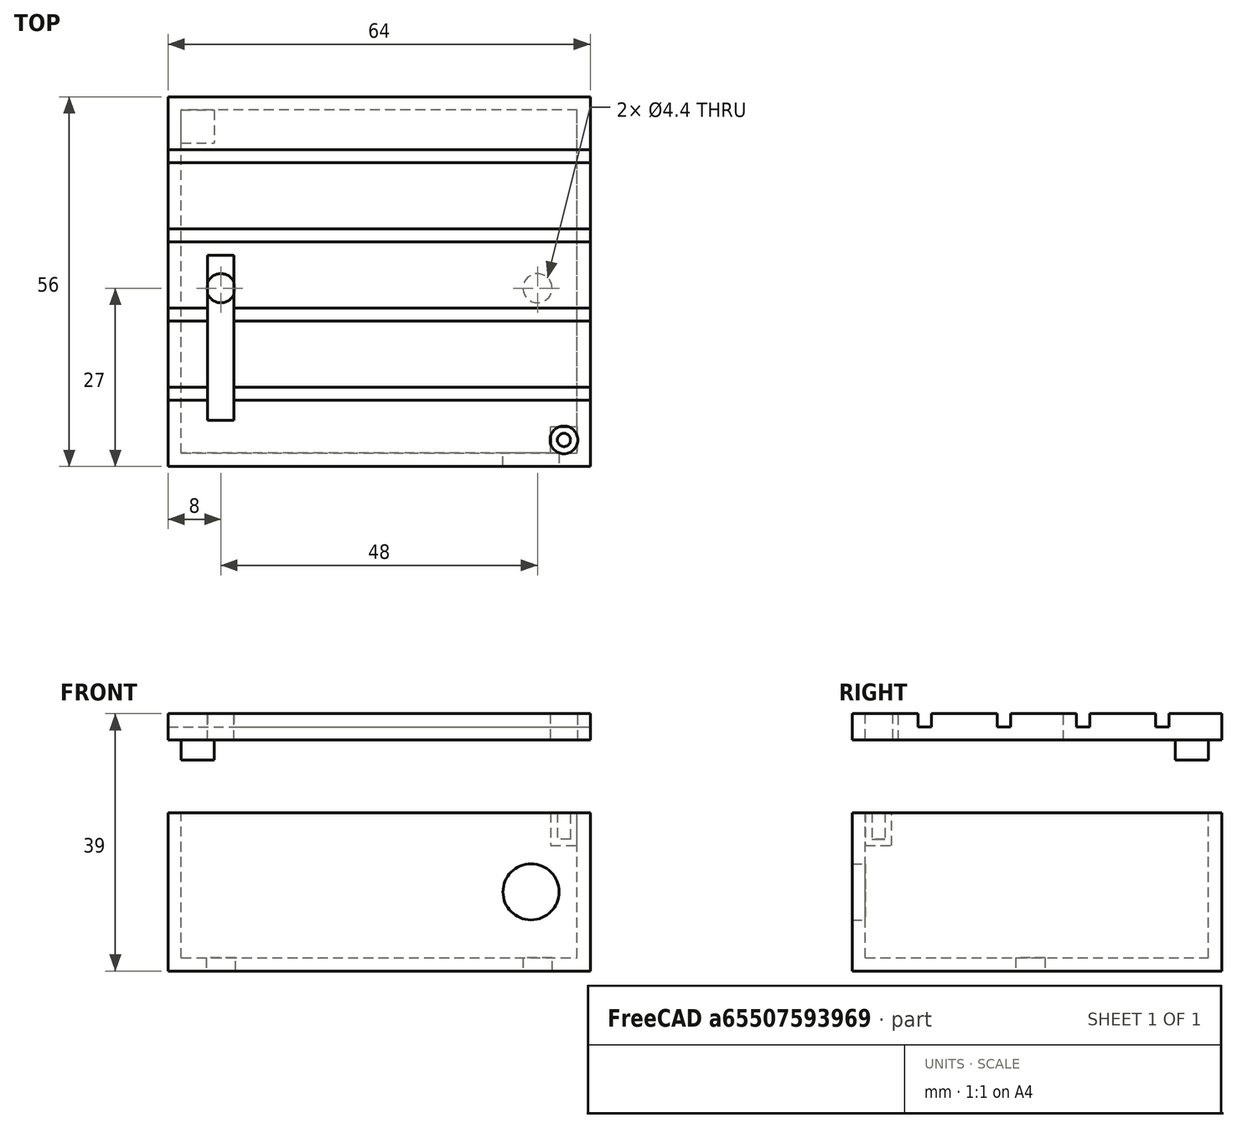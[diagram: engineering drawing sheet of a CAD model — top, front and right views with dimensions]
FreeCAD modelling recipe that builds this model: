
FCSTD DOCUMENT  (FreeCAD 0.20R29603 (Git))
Label: boxv1
License: All rights reserved
LicenseURL: http://en.wikipedia.org/wiki/All_rights_reserved
objects: Part::Box×11, Part::Cut×7, Part::Cylinder×5, Part::MultiFuse×2, App::DocumentObjectGroup×2
note: 25 computed .brp shape members not serialized (recipe doc carries the construction recipe); baked Part::Feature solids carry a one-line shape summary decoded from their .brp

FEATURE [Part::Box] Box  label="Cube"
  AttacherType = Attacher::AttachEngine3D
  Height = 24
  Length = 64
  Width = 56
FEATURE [Part::Box] Box001  label="Cube001"
  AttacherType = Attacher::AttachEngine3D
  Height = 24
  Length = 60
  Placement = pos=(2,2,2) rot=(0,0,1;0rad)
  Width = 52
FEATURE [Part::Cut] Cut
  Base = -> Box
  Tool = -> Box001
FEATURE [Part::Cylinder] Cylinder
  Angle = 360
  AttacherType = Attacher::AttachEngine3D
  FirstAngle = 0
  Height = 10
  Placement = pos=(55,4,12) rot=(1,0,0;1.5708rad)
  Radius = 4.25
  SecondAngle = 0
FEATURE [Part::Box] Box002  label="Cube002"
  AttacherType = Attacher::AttachEngine3D
  Height = 2
  Length = 64
  Placement = pos=(0,0,34) rot=(0,0,1;0rad)
  Width = 56
FEATURE [Part::Cut] Cut001
  Base = -> Cut
  Tool = -> Cylinder
FEATURE [Part::Box] Box003  label="Cube003"
  AttacherType = Attacher::AttachEngine3D
  Height = 5
  Length = 5
  Placement = pos=(2,49,31) rot=(0,0,1;0rad)
  Width = 5
FEATURE [Part::Box] Box004  label="Cube004"
  AttacherType = Attacher::AttachEngine3D
  Height = 5
  Length = 5
  Placement = pos=(58,1,19) rot=(0,0,1;0rad)
  Width = 5
FEATURE [Part::Cylinder] Cylinder001
  Angle = 360
  AttacherType = Attacher::AttachEngine3D
  FirstAngle = 0
  Height = 10
  Placement = pos=(60,4,30) rot=(0,0,1;0rad)
  Radius = 2.1
  SecondAngle = 0
FEATURE [Part::Box] Box005  label="Cube005"
  AttacherType = Attacher::AttachEngine3D
  Height = 10
  Length = 4
  Placement = pos=(6,7,33) rot=(0,0,1;0rad)
  Width = 25
FEATURE [Part::Cylinder] Cylinder002
  Angle = 360
  AttacherType = Attacher::AttachEngine3D
  FirstAngle = 0
  Height = 10
  Placement = pos=(60,4,20) rot=(0,0,1;0rad)
  Radius = 1
  SecondAngle = 0
FEATURE [Part::MultiFuse] Fusion001
  Shapes = -> [Cut001,Box004]
FEATURE [Part::Cut] Cut004
  Base = -> Fusion001
  Tool = -> Cylinder002
FEATURE [Part::Box] Box006  label="Cube006"
  AttacherType = Attacher::AttachEngine3D
  Height = 2
  Length = 64
  Placement = pos=(0,0,36) rot=(0,0,1;0rad)
  Width = 10
FEATURE [Part::Box] Box007  label="Cube007"
  AttacherType = Attacher::AttachEngine3D
  Height = 2
  Length = 64
  Placement = pos=(0,48,36) rot=(0,0,1;0rad)
  Width = 8
FEATURE [Part::Box] Box008  label="Cube008"
  AttacherType = Attacher::AttachEngine3D
  Height = 2
  Length = 64
  Placement = pos=(0,12,36) rot=(0,0,1;0rad)
  Width = 10
FEATURE [Part::Box] Box009  label="Cube009"
  AttacherType = Attacher::AttachEngine3D
  Height = 2
  Length = 64
  Placement = pos=(0,24,36) rot=(0,0,1;0rad)
  Width = 10
FEATURE [Part::Box] Box010  label="Cube010"
  AttacherType = Attacher::AttachEngine3D
  Height = 2
  Length = 64
  Placement = pos=(0,36,36) rot=(0,0,1;0rad)
  Width = 10
FEATURE [Part::MultiFuse] Fusion
  Shapes = -> [Box003,Box006,Box007,Box008,Box009,Box010,Box002]
FEATURE [Part::Cut] Cut003
  Base = -> Fusion
  Placement = pos=(0,0,1) rot=(0,0,1;0rad)
  Tool = -> Box005
FEATURE [Part::Cut] Cut005
  Base = -> Cut003
  Tool = -> Cylinder001
FEATURE [App::DocumentObjectGroup] Group001  label="lid"
  Group = -> [Cut005]
FEATURE [Part::Cylinder] Cylinder003
  Angle = 360
  AttacherType = Attacher::AttachEngine3D
  FirstAngle = 0
  Height = 10
  Placement = pos=(56,27,-1) rot=(0,0,1;0rad)
  Radius = 2.2
  SecondAngle = 0
FEATURE [Part::Cylinder] Cylinder004
  Angle = 360
  AttacherType = Attacher::AttachEngine3D
  FirstAngle = 0
  Height = 10
  Placement = pos=(8,27,-1) rot=(0,0,1;0rad)
  Radius = 2.2
  SecondAngle = 0
FEATURE [Part::Cut] Cut006
  Base = -> Cut004
  Tool = -> Cylinder003
FEATURE [Part::Cut] Cut007
  Base = -> Cut006
  Tool = -> Cylinder004
FEATURE [App::DocumentObjectGroup] Group  label="body"
  Group = -> [Cut007]
